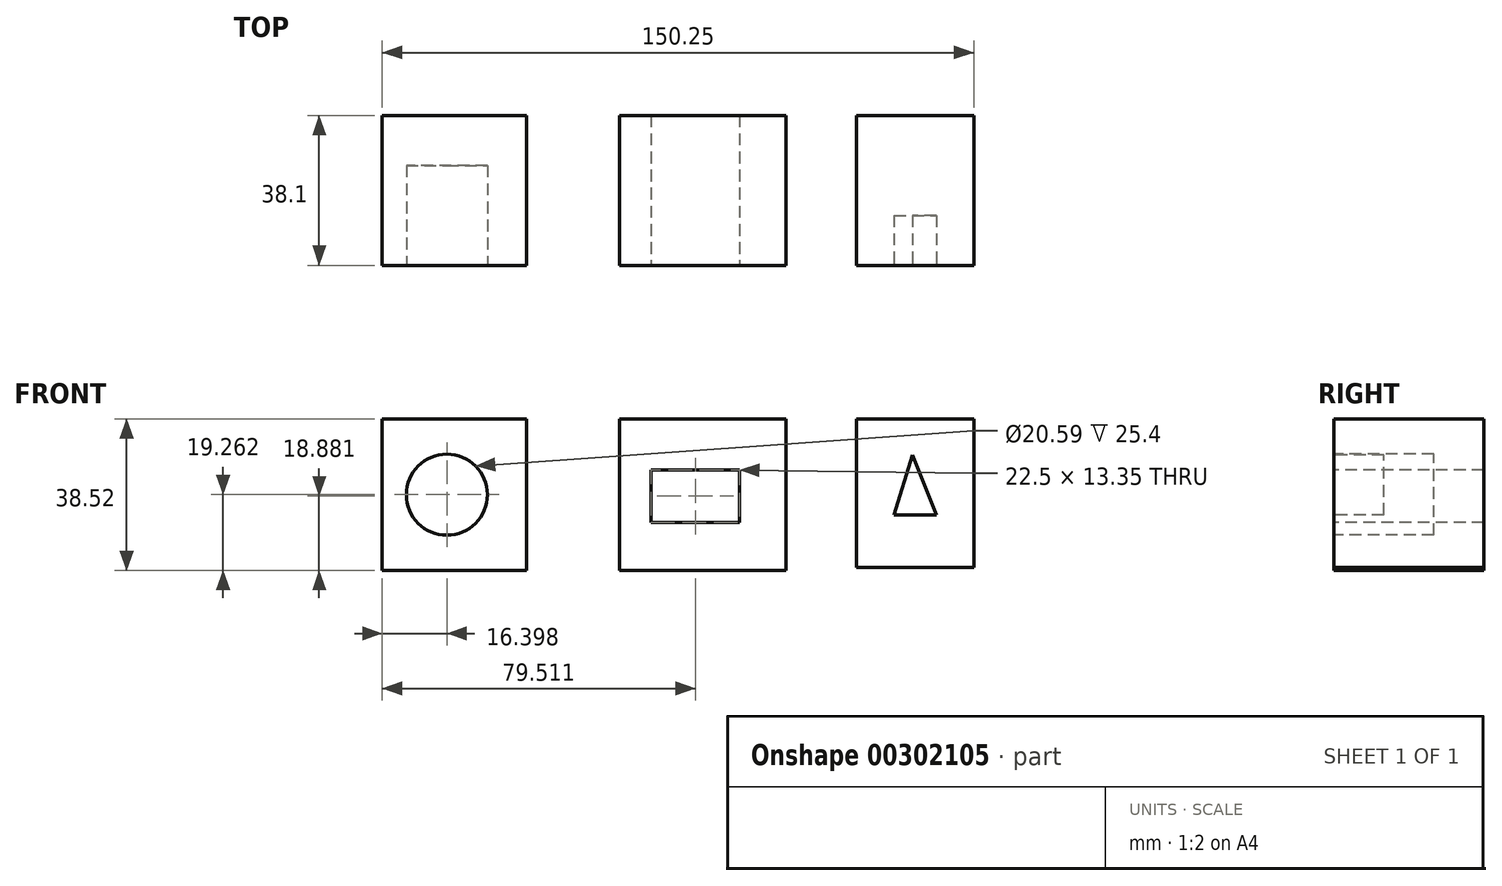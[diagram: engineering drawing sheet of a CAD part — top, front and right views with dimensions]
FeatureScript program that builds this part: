
annotation { "Feature Type Name" : "Feature", "Feature Type Description" : "" }
export const myFeature = defineFeature(function(context is Context, id is Id, definition is map)
    precondition{}
    {
        {
            var Q0;
            Q0=qCreatedBy(makeId("Front.planeOp"),FACE);
            var sketch = newSketch(context, id + "F0", { "sketchPlane" : qUnion([Q0])});
            skLineSegment(sketch, "E0.bottom", {"start": v(-76.27, 0) * mm, "end": v(-39.66, 0) * mm});
            skLineSegment(sketch, "E0.top", {"start": v(-76.27, -38.52) * mm, "end": v(-39.66, -38.52) * mm});
            skLineSegment(sketch, "E0.left", {"start": v(-76.27, 0) * mm, "end": v(-76.27, -38.52) * mm});
            skLineSegment(sketch, "E0.right", {"start": v(-39.66, 0) * mm, "end": v(-39.66, -38.52) * mm});
            skSolve(sketch);
        }
        {
            var Q0;
            Q0=qCreatedBy(makeId("Front.planeOp"),FACE);
            var sketch = newSketch(context, id + "F1", { "sketchPlane" : qUnion([Q0])});
            skLineSegment(sketch, "E1", {"start": v(-40.42, 0) * mm, "end": v(-16.02, 0) * mm});
            skSolve(sketch);
        }
        {
            var Q0;
            Q0=qCreatedBy(makeId("Front.planeOp"),FACE);
            var sketch = newSketch(context, id + "F2", { "sketchPlane" : qUnion([Q0])});
            skLineSegment(sketch, "E2.bottom", {"start": v(-16.02, 0) * mm, "end": v(26.31, 0) * mm});
            skLineSegment(sketch, "E2.top", {"start": v(-16.02, -38.52) * mm, "end": v(26.31, -38.52) * mm});
            skLineSegment(sketch, "E2.left", {"start": v(-16.02, 0) * mm, "end": v(-16.02, -38.52) * mm});
            skLineSegment(sketch, "E2.right", {"start": v(26.31, 0) * mm, "end": v(26.31, -38.52) * mm});
            skSolve(sketch);
        }
        {
            var Q0;
            Q0=qCreatedBy(makeId("Front.planeOp"),FACE);
            var sketch = newSketch(context, id + "F3", { "sketchPlane" : qUnion([Q0])});
            skLineSegment(sketch, "E3", {"start": v(25.93, 0) * mm, "end": v(44.24, 0) * mm});
            skSolve(sketch);
        }
        {
            var Q0;
            Q0=qCreatedBy(makeId("Front.planeOp"),FACE);
            var sketch = newSketch(context, id + "F4", { "sketchPlane" : qUnion([Q0])});
            skLineSegment(sketch, "E4.bottom", {"start": v(44.24, 0) * mm, "end": v(73.98, 0) * mm});
            skLineSegment(sketch, "E4.top", {"start": v(44.24, -37.75) * mm, "end": v(73.98, -37.75) * mm});
            skLineSegment(sketch, "E4.left", {"start": v(44.24, 0) * mm, "end": v(44.24, -37.75) * mm});
            skLineSegment(sketch, "E4.right", {"start": v(73.98, 0) * mm, "end": v(73.98, -37.75) * mm});
            skSolve(sketch);
        }
        {
            var Q0;
            Q0=makeQuery(id+"F0.imprint","IMPRINT",FACE,{"disambiguationData":[TD([[makeQuery(id+"F0.imprint","IMPRINT",EDGE,{"derivedFrom":sQuery(id+"F0.wireOp",EDGE,"E0.bottom")}),-1.0]])]});
            extrude(context, id + "F5", {"entities" : qUnion([Q0]), "depth" : 38.1 * mm});
        }
        {
            var Q0;
            Q0=makeQuery(id+"F2.imprint","IMPRINT",FACE,{"disambiguationData":[TD([[makeQuery(id+"F2.imprint","IMPRINT",EDGE,{"derivedFrom":sQuery(id+"F2.wireOp",EDGE,"E2.bottom")}),-1.0]])]});
            extrude(context, id + "F6", {"entities" : qUnion([Q0]), "depth" : 38.1 * mm});
        }
        {
            var Q0;
            Q0=makeQuery(id+"F4.imprint","IMPRINT",FACE,{"disambiguationData":[TD([[makeQuery(id+"F4.imprint","IMPRINT",EDGE,{"derivedFrom":sQuery(id+"F4.wireOp",EDGE,"E4.bottom")}),-1.0]])]});
            extrude(context, id + "F7", {"entities" : qUnion([Q0]), "depth" : 38.1 * mm});
        }
        {
            var Q0;
            Q0=sQuery(id+"F1.wireOp",EDGE,"E1");
            extrude(context, id + "F8", {"bodyType" : ToolBodyType.SURFACE, "surfaceEntities" : qUnion([Q0]), "depth" : 25.4 * mm});
        }
        {
            var Q0;
            Q0=sQuery(id+"F3.wireOp",EDGE,"E3");
            extrude(context, id + "F9", {"bodyType" : ToolBodyType.SURFACE, "surfaceEntities" : qUnion([Q0]), "depth" : 25.4 * mm});
        }
        {
            var Q0;
            Q0=makeQuery(id+"F5.opExtrude","CAP_FACE",FACE,{"disambiguationData":[OSD([sQuery(id+"F0.wireOp",EDGE,"E0.bottom"),sQuery(id+"F0.wireOp",EDGE,"E0.top"),sQuery(id+"F0.wireOp",EDGE,"E0.left"),sQuery(id+"F0.wireOp",EDGE,"E0.right")])],"isStart":false});
            var sketch = newSketch(context, id + "F10", { "sketchPlane" : qUnion([Q0])});
            skCircle(sketch, "E5", {"center": v(-59.87, -19.26) * mm, "radius": 10.3 * mm});
            skPoint(sketch, "E5.centerSnap0", {"position": v(-76.27, -19.26) * mm});
            skPoint(sketch, "E5.perimeterSnap0", {"position": v(-76.27, -19.26) * mm});
            skSolve(sketch);
        }
        {
            var Q0;
            Q0=makeQuery(id+"F6.opExtrude","CAP_FACE",FACE,{"disambiguationData":[OSD([sQuery(id+"F2.wireOp",EDGE,"E2.bottom"),sQuery(id+"F2.wireOp",EDGE,"E2.top"),sQuery(id+"F2.wireOp",EDGE,"E2.left"),sQuery(id+"F2.wireOp",EDGE,"E2.right")])],"isStart":false});
            var sketch = newSketch(context, id + "F11", { "sketchPlane" : qUnion([Q0])});
            skLineSegment(sketch, "E6.bottom", {"start": v(-8, -12.97) * mm, "end": v(14.5, -12.97) * mm});
            skLineSegment(sketch, "E6.top", {"start": v(-8, -26.31) * mm, "end": v(14.5, -26.31) * mm});
            skLineSegment(sketch, "E6.left", {"start": v(-8, -12.97) * mm, "end": v(-8, -26.31) * mm});
            skLineSegment(sketch, "E6.right", {"start": v(14.5, -12.97) * mm, "end": v(14.5, -26.31) * mm});
            skSolve(sketch);
        }
        {
            var Q0;
            Q0=makeQuery(id+"F7.opExtrude","CAP_FACE",FACE,{"disambiguationData":[OSD([sQuery(id+"F4.wireOp",EDGE,"E4.bottom"),sQuery(id+"F4.wireOp",EDGE,"E4.top"),sQuery(id+"F4.wireOp",EDGE,"E4.left"),sQuery(id+"F4.wireOp",EDGE,"E4.right")])],"isStart":false});
            var sketch = newSketch(context, id + "F12", { "sketchPlane" : qUnion([Q0])});
            skLineSegment(sketch, "E7", {"start": v(53.77, -24.4) * mm, "end": v(64.45, -24.4) * mm});
            skLineSegment(sketch, "E8", {"start": v(64.45, -24.4) * mm, "end": v(58.35, -9.15) * mm});
            skLineSegment(sketch, "E9", {"start": v(53.77, -24.4) * mm, "end": v(58.35, -9.15) * mm});
            skSolve(sketch);
        }
        {
            var Q0;
            Q0=makeQuery(id+"F12.imprint","IMPRINT",FACE,{"disambiguationData":[TD([[makeQuery(id+"F12.imprint","IMPRINT",EDGE,{"derivedFrom":sQuery(id+"F12.wireOp",EDGE,"E7")}),1.0]])]});
            extrude(context, id + "F13", {"entities" : qUnion([Q0]), "operationType" : NewBodyOperationType.REMOVE, "oppositeDirection" : true, "depth" : 12.7 * mm});
        }
        {
            var Q0;
            Q0=makeQuery(id+"F11.imprint","IMPRINT",FACE,{"disambiguationData":[TD([[makeQuery(id+"F11.imprint","IMPRINT",EDGE,{"derivedFrom":sQuery(id+"F11.wireOp",EDGE,"E6.bottom")}),-1.0]])]});
            extrude(context, id + "F14", {"entities" : qUnion([Q0]), "operationType" : NewBodyOperationType.REMOVE, "oppositeDirection" : true, "depth" : 50.8 * mm});
        }
        {
            var Q0;
            Q0=makeQuery(id+"F10.imprint","IMPRINT",FACE,{"disambiguationData":[TD([[makeQuery(id+"F10.imprint","IMPRINT",EDGE,{"derivedFrom":sQuery(id+"F10.wireOp",EDGE,"E5")}),1.0]])]});
            extrude(context, id + "F15", {"entities" : qUnion([Q0]), "operationType" : NewBodyOperationType.REMOVE, "oppositeDirection" : true, "depth" : 25.4 * mm});
        }
    });
